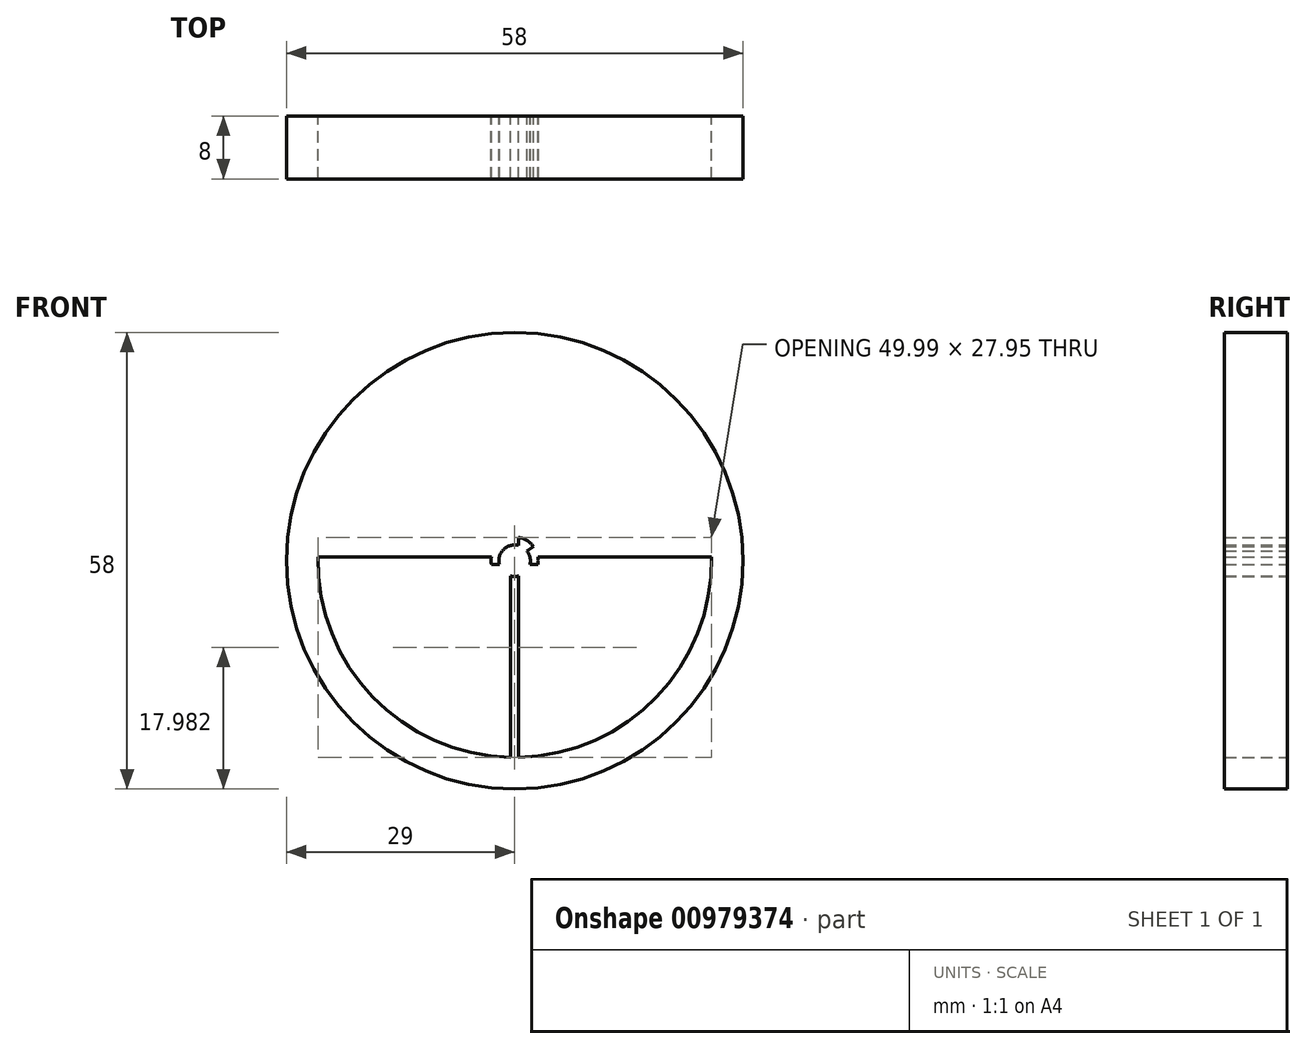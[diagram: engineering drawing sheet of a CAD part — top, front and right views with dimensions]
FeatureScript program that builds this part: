
annotation { "Feature Type Name" : "Feature", "Feature Type Description" : "" }
export const myFeature = defineFeature(function(context is Context, id is Id, definition is map)
    precondition{}
    {
        {
            var Q0;
            Q0=qCreatedBy(makeId("Front.planeOp"),FACE);
            var sketch = newSketch(context, id + "F0", { "sketchPlane" : qUnion([Q0])});
            skCircle(sketch, "E0", {"center": v(0, 0) * mm, "radius": 29 * mm});
            skCircle(sketch, "E1", {"center": v(0, 0) * mm, "radius": 2 * mm});
            skCircle(sketch, "E2", {"center": v(0, 0) * mm, "radius": 25 * mm});
            skCircle(sketch, "E3", {"center": v(0, 0) * mm, "radius": 3 * mm});
            skLineSegment(sketch, "E4", {"start": v(-0.5, 25) * mm, "end": v(-0.5, -25) * mm});
            skLineSegment(sketch, "E5", {"start": v(0.5, 25) * mm, "end": v(0.5, -25) * mm});
            skLineSegment(sketch, "E6", {"start": v(-25, 0.5) * mm, "end": v(25, 0.5) * mm});
            skLineSegment(sketch, "E7", {"start": v(-25, -0.5) * mm, "end": v(25, -0.5) * mm});
            skLineSegment(sketch, "E8", {"start": v(0, 0) * mm, "end": v(1.6, 2.54) * mm});
            skLineSegment(sketch, "E9", {"start": v(0, 0) * mm, "end": v(2.39, 1.81) * mm});
            skSolve(sketch);
        }
        {
            var Q0;
            Q0=makeQuery(id+"F0.imprint","IMPRINT",FACE,{"disambiguationData":[TD([[makeQuery(id+"F0.imprint","IMPRINT",EDGE,{"derivedFrom":sQuery(id+"F0.wireOp",EDGE,"E0")}),1.0]])]});
            var Q1;
            {var subQ0=sQuery(id+"F0.wireOp",EDGE,"E4");var subQ1=sQuery(id+"F0.wireOp",EDGE,"E2");var subQ2=makeQuery(id+"F0.imprint","INTERSECT",VERTEX,{"disambiguationData":[OD(0.0)],"derivedFrom":[subQ1,subQ0]});Q1=makeQuery(id+"F0.imprint","IMPRINT",FACE,{"disambiguationData":[TD([[makeQuery(id+"F0.imprint","IMPRINT",EDGE,{"disambiguationData":[TD([[subQ2,1.0]])],"derivedFrom":subQ1}),1.0]])]});}
            var Q2;
            {var subQ0=sQuery(id+"F0.wireOp",EDGE,"E4");var subQ1=sQuery(id+"F0.wireOp",EDGE,"E1");var subQ2=makeQuery(id+"F0.imprint","INTERSECT",VERTEX,{"disambiguationData":[OD(0.0)],"derivedFrom":[subQ1,subQ0]});Q2=makeQuery(id+"F0.imprint","IMPRINT",FACE,{"disambiguationData":[TD([[makeQuery(id+"F0.imprint","IMPRINT",EDGE,{"disambiguationData":[TD([[subQ2,-1.0]])],"derivedFrom":subQ1}),-1.0]])]});}
            var Q3;
            {var subQ0=sQuery(id+"F0.wireOp",EDGE,"E4");var subQ1=sQuery(id+"F0.wireOp",EDGE,"E1");var subQ2=makeQuery(id+"F0.imprint","INTERSECT",VERTEX,{"disambiguationData":[OD(0.0)],"derivedFrom":[subQ1,subQ0]});Q3=makeQuery(id+"F0.imprint","IMPRINT",FACE,{"disambiguationData":[TD([[makeQuery(id+"F0.imprint","IMPRINT",EDGE,{"disambiguationData":[TD([[subQ2,1.0]])],"derivedFrom":subQ1}),-1.0]])]});}
            var Q4;
            {var subQ0=sQuery(id+"F0.wireOp",EDGE,"E5");var subQ1=sQuery(id+"F0.wireOp",EDGE,"E1");var subQ2=makeQuery(id+"F0.imprint","INTERSECT",VERTEX,{"disambiguationData":[OD(0.0)],"derivedFrom":[subQ1,subQ0]});Q4=makeQuery(id+"F0.imprint","IMPRINT",FACE,{"disambiguationData":[TD([[makeQuery(id+"F0.imprint","IMPRINT",EDGE,{"disambiguationData":[TD([[subQ2,1.0]])],"derivedFrom":subQ1}),-1.0]])]});}
            var Q5;
            {var subQ0=sQuery(id+"F0.wireOp",EDGE,"E4");var subQ1=sQuery(id+"F0.wireOp",EDGE,"E1");var subQ2=makeQuery(id+"F0.imprint","INTERSECT",VERTEX,{"disambiguationData":[OD(1.0)],"derivedFrom":[subQ1,subQ0]});Q5=makeQuery(id+"F0.imprint","IMPRINT",FACE,{"disambiguationData":[TD([[makeQuery(id+"F0.imprint","IMPRINT",EDGE,{"disambiguationData":[TD([[subQ2,-1.0]])],"derivedFrom":subQ1}),-1.0]])]});}
            var Q6;
            {var subQ0=sQuery(id+"F0.wireOp",EDGE,"E4");var subQ1=sQuery(id+"F0.wireOp",EDGE,"E2");var subQ2=makeQuery(id+"F0.imprint","INTERSECT",VERTEX,{"disambiguationData":[OD(1.0)],"derivedFrom":[subQ1,subQ0]});Q6=makeQuery(id+"F0.imprint","IMPRINT",FACE,{"disambiguationData":[TD([[makeQuery(id+"F0.imprint","IMPRINT",EDGE,{"disambiguationData":[TD([[subQ2,-1.0]])],"derivedFrom":subQ1}),1.0]])]});}
            var Q7;
            {var subQ0=sQuery(id+"F0.wireOp",EDGE,"E6");var subQ1=sQuery(id+"F0.wireOp",EDGE,"E2");var subQ2=makeQuery(id+"F0.imprint","INTERSECT",VERTEX,{"disambiguationData":[OD(0.0)],"derivedFrom":[subQ1,subQ0]});Q7=makeQuery(id+"F0.imprint","IMPRINT",FACE,{"disambiguationData":[TD([[makeQuery(id+"F0.imprint","IMPRINT",EDGE,{"disambiguationData":[TD([[subQ2,-1.0]])],"derivedFrom":subQ1}),1.0]])]});}
            var Q8;
            {var subQ0=sQuery(id+"F0.wireOp",EDGE,"E6");var subQ1=sQuery(id+"F0.wireOp",EDGE,"E1");var subQ2=makeQuery(id+"F0.imprint","INTERSECT",VERTEX,{"disambiguationData":[OD(1.0)],"derivedFrom":[subQ1,subQ0]});Q8=makeQuery(id+"F0.imprint","IMPRINT",FACE,{"disambiguationData":[TD([[makeQuery(id+"F0.imprint","IMPRINT",EDGE,{"disambiguationData":[TD([[subQ2,-1.0]])],"derivedFrom":subQ1}),-1.0]])]});}
            var Q9;
            {var subQ0=sQuery(id+"F0.wireOp",EDGE,"E7");var subQ1=sQuery(id+"F0.wireOp",EDGE,"E1");var subQ2=makeQuery(id+"F0.imprint","INTERSECT",VERTEX,{"disambiguationData":[OD(0.0)],"derivedFrom":[subQ1,subQ0]});Q9=makeQuery(id+"F0.imprint","IMPRINT",FACE,{"disambiguationData":[TD([[makeQuery(id+"F0.imprint","IMPRINT",EDGE,{"disambiguationData":[TD([[subQ2,-1.0]])],"derivedFrom":subQ1}),-1.0]])]});}
            var Q10;
            {var subQ0=sQuery(id+"F0.wireOp",EDGE,"E5");var subQ1=sQuery(id+"F0.wireOp",EDGE,"E1");var subQ2=makeQuery(id+"F0.imprint","INTERSECT",VERTEX,{"disambiguationData":[OD(1.0)],"derivedFrom":[subQ1,subQ0]});Q10=makeQuery(id+"F0.imprint","IMPRINT",FACE,{"disambiguationData":[TD([[makeQuery(id+"F0.imprint","IMPRINT",EDGE,{"disambiguationData":[TD([[subQ2,-1.0]])],"derivedFrom":subQ1}),-1.0]])]});}
            var Q11;
            {var subQ0=sQuery(id+"F0.wireOp",EDGE,"E6");var subQ1=sQuery(id+"F0.wireOp",EDGE,"E2");var subQ2=makeQuery(id+"F0.imprint","INTERSECT",VERTEX,{"disambiguationData":[OD(1.0)],"derivedFrom":[subQ1,subQ0]});Q11=makeQuery(id+"F0.imprint","IMPRINT",FACE,{"disambiguationData":[TD([[makeQuery(id+"F0.imprint","IMPRINT",EDGE,{"disambiguationData":[TD([[subQ2,1.0]])],"derivedFrom":subQ1}),1.0]])]});}
            var Q12;
            {var subQ0=sQuery(id+"F0.wireOp",EDGE,"E6");var subQ1=sQuery(id+"F0.wireOp",EDGE,"E1");var subQ2=makeQuery(id+"F0.imprint","INTERSECT",VERTEX,{"disambiguationData":[OD(0.0)],"derivedFrom":[subQ1,subQ0]});Q12=makeQuery(id+"F0.imprint","IMPRINT",FACE,{"disambiguationData":[TD([[makeQuery(id+"F0.imprint","IMPRINT",EDGE,{"disambiguationData":[TD([[subQ2,1.0]])],"derivedFrom":subQ1}),-1.0]])]});}
            var Q13;
            {var subQ0=sQuery(id+"F0.wireOp",EDGE,"E9");var subQ1=sQuery(id+"F0.wireOp",EDGE,"E1");var subQ2=makeQuery(id+"F0.imprint","INTERSECT",VERTEX,{"derivedFrom":[subQ1,subQ0]});Q13=makeQuery(id+"F0.imprint","IMPRINT",FACE,{"disambiguationData":[TD([[makeQuery(id+"F0.imprint","IMPRINT",EDGE,{"disambiguationData":[TD([[subQ2,1.0]])],"derivedFrom":subQ1}),-1.0]])]});}
            extrude(context, id + "F1", {"entities" : qUnion([Q0, Q1, Q2, Q3, Q4, Q5, Q6, Q7, Q8, Q9, Q10, Q11, Q12, Q13]), "depth" : 8 * mm, "offsetDistance" : 25 * mm});
        }
    });
